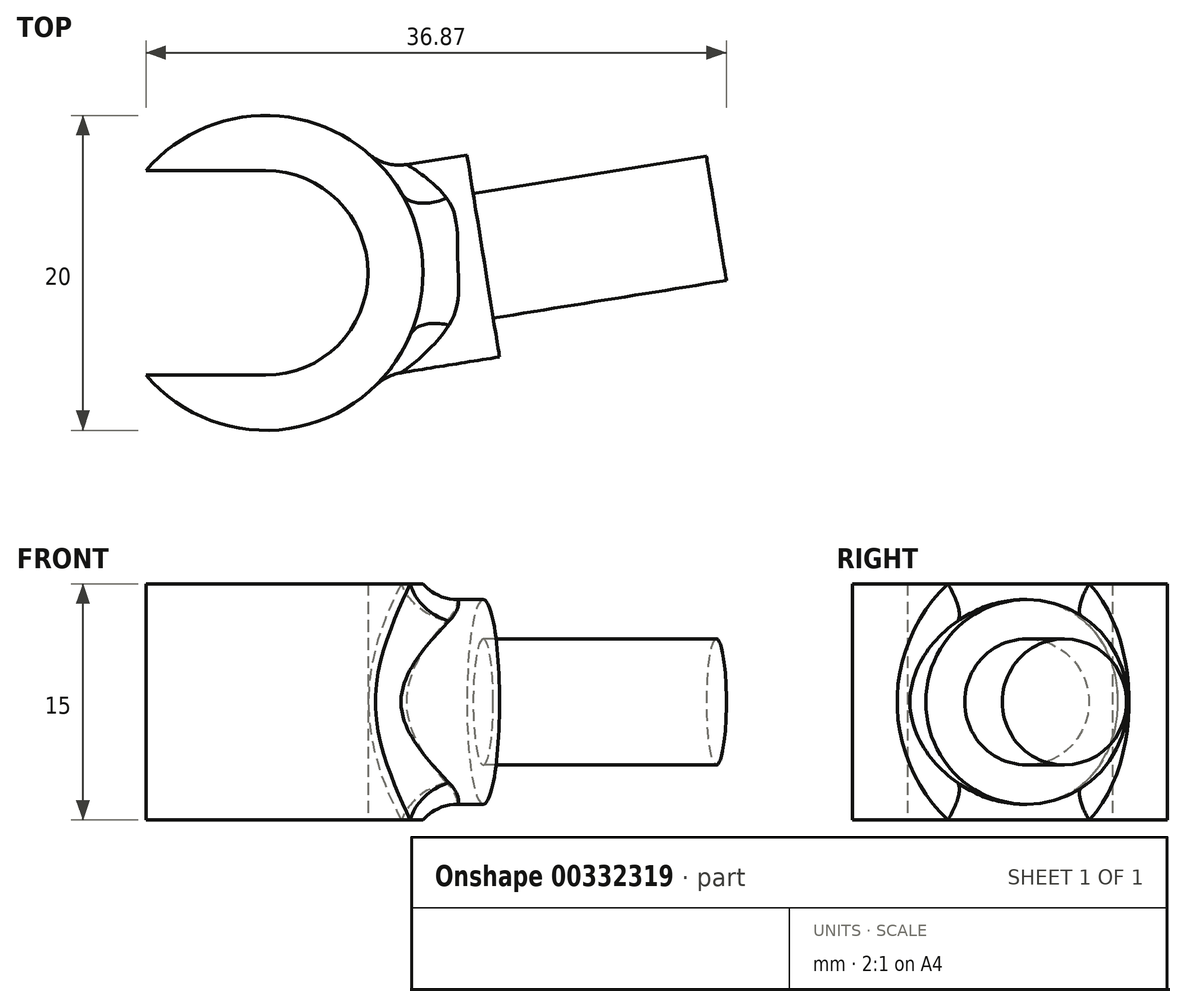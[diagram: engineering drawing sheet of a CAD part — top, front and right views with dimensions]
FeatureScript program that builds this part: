
annotation { "Feature Type Name" : "Feature", "Feature Type Description" : "" }
export const myFeature = defineFeature(function(context is Context, id is Id, definition is map)
    precondition{}
    {
        {
            var Q0;
            Q0=qCreatedBy(makeId("Top.planeOp"),FACE);
            var sketch = newSketch(context, id + "F0", { "sketchPlane" : qUnion([Q0])});
            skArc(sketch, "E0", {"start": v(-7.6, -6.5) * mm, "mid": v(10, 0) * mm, "end": v(-7.6, 6.5) * mm});
            skArc(sketch, "E1", {"start": v(0, -6.5) * mm, "mid": v(6.5, 0) * mm, "end": v(0, 6.5) * mm});
            skLineSegment(sketch, "E2", {"start": v(0, 6.5) * mm, "end": v(-7.6, 6.5) * mm});
            skLineSegment(sketch, "E3", {"start": v(0, -6.5) * mm, "end": v(-7.6, -6.5) * mm});
            skSolve(sketch);
        }
        {
            var Q0;
            Q0=makeQuery(id+"F0.imprint","IMPRINT",FACE,{"disambiguationData":[TD([[makeQuery(id+"F0.imprint","IMPRINT",EDGE,{"derivedFrom":sQuery(id+"F0.wireOp",EDGE,"E0")}),1.0]])]});
            extrude(context, id + "F1", {"entities" : qUnion([Q0]), "depth" : 15 * mm, "symmetric" : true});
        }
        {
            var Q0;
            Q0=qCreatedBy(makeId("Top.planeOp"),FACE);
            var sketch = newSketch(context, id + "F2", { "sketchPlane" : qUnion([Q0])});
            skLineSegment(sketch, "E4", {"start": v(7.1, 0) * mm, "end": v(28.63, 3.47) * mm});
            skLineSegment(sketch, "E5", {"start": v(28.63, 3.47) * mm, "end": v(29.27, -0.48) * mm});
            skLineSegment(sketch, "E6", {"start": v(29.27, -0.48) * mm, "end": v(14.46, -2.87) * mm});
            skLineSegment(sketch, "E7", {"start": v(14.46, -2.87) * mm, "end": v(14.86, -5.33) * mm});
            skLineSegment(sketch, "E8", {"start": v(14.86, -5.33) * mm, "end": v(5.48, -6.84) * mm});
            skLineSegment(sketch, "E9", {"start": v(5.48, -6.84) * mm, "end": v(7.1, 0) * mm});
            skSolve(sketch);
        }
        {
            var Q0;
            Q0=makeQuery(id+"F2.imprint","IMPRINT",FACE,{"disambiguationData":[TD([[makeQuery(id+"F2.imprint","IMPRINT",EDGE,{"derivedFrom":sQuery(id+"F2.wireOp",EDGE,"E4")}),-1.0]])]});
            var Q1;
            Q1=sQuery(id+"F2.wireOp",EDGE,"E4");
            revolve(context, id + "F3", {"operationType" : NewBodyOperationType.ADD, "entities" : qUnion([Q0]), "axis" : qUnion([Q1]), "revolveType" : RevolveType.FULL});
        }
        {
            var Q0;
            Q0=qCreatedBy(makeId("Top.planeOp"),FACE);
            var sketch = newSketch(context, id + "F4", { "sketchPlane" : qUnion([Q0])});
            skCircle(sketch, "E10", {"center": v(0, 0) * mm, "radius": 6.5 * mm});
            skSolve(sketch);
        }
        {
            var Q0;
            Q0=qSketchRegion(id+"F4",true);
            extrude(context, id + "F5", {"entities" : qUnion([Q0]), "operationType" : NewBodyOperationType.REMOVE, "oppositeDirection" : true, "depth" : 25 * mm, "symmetric" : true});
        }
        {
            var Q0;
            Q0=makeQuery(id+"F3.boolean.opBoolean","INTERSECT",EDGE,{"derivedFrom":[makeQuery(id+"F1.opExtrude","SWEPT_FACE",FACE,{"disambiguationData":[OSD([sQuery(id+"F0.wireOp",EDGE,"E0")])]}),makeQuery(id+"F3.opRevolve","SWEPT_FACE",FACE,{"disambiguationData":[OSD([sQuery(id+"F2.wireOp",EDGE,"E8")])]})]});
            fillet(context, id + "F6", {"entities" : qUnion([Q0]), "radius" : 3 * mm, "allowEdgeOverflow" : false});
        }
    });
